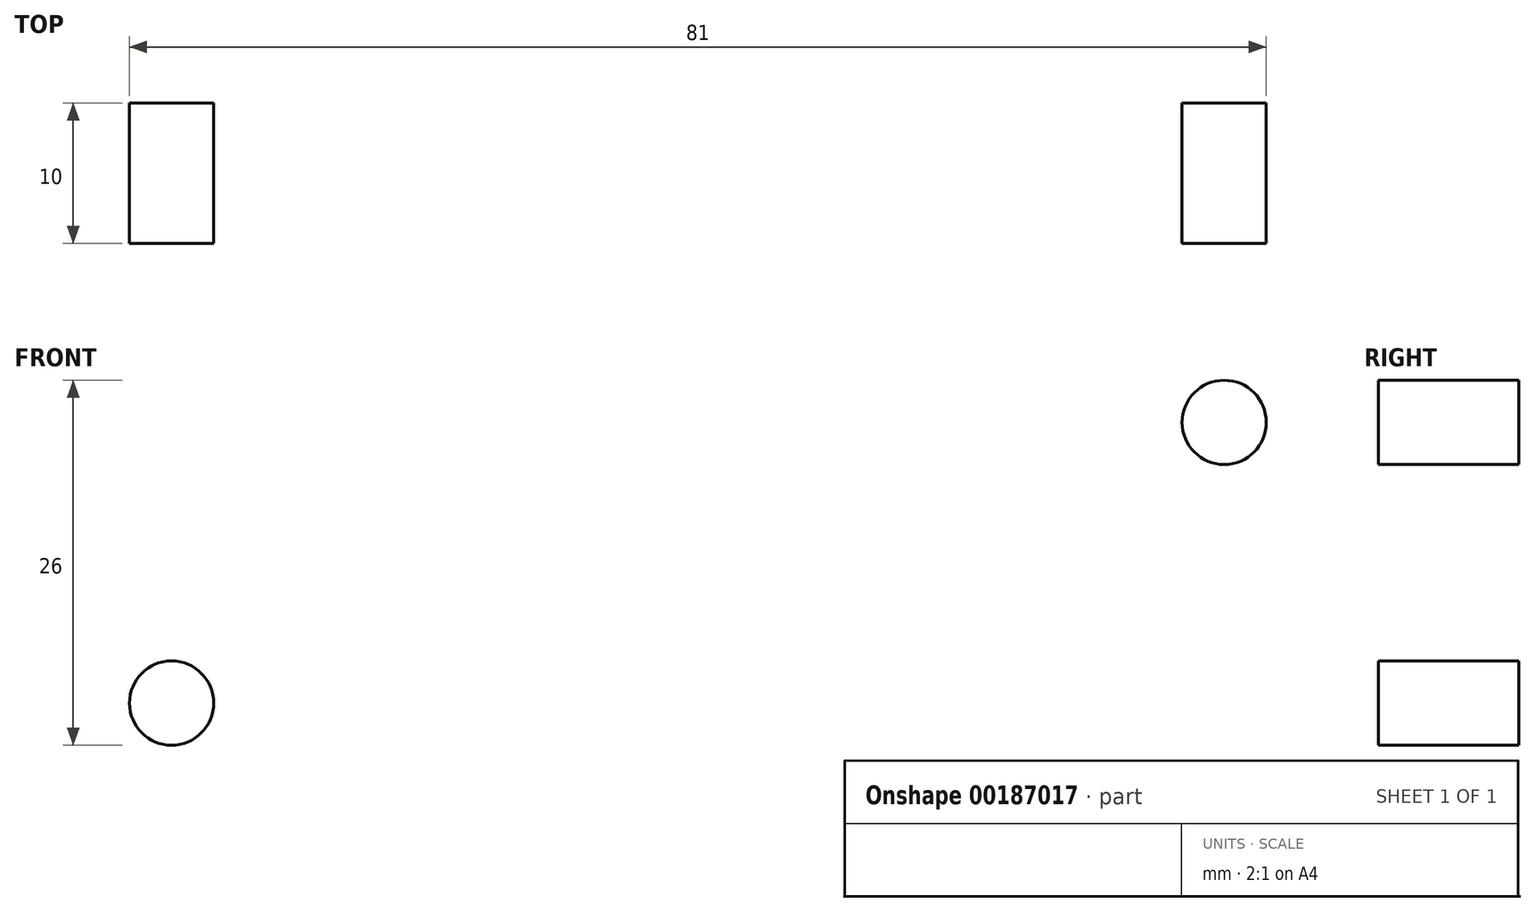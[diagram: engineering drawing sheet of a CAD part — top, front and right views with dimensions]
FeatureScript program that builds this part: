
annotation { "Feature Type Name" : "Feature", "Feature Type Description" : "" }
export const myFeature = defineFeature(function(context is Context, id is Id, definition is map)
    precondition{}
    {
        {
            var Q0;
            Q0=qCreatedBy(makeId("Front.planeOp"),FACE);
            var sketch = newSketch(context, id + "F0", { "sketchPlane" : qUnion([Q0])});
            skLineSegment(sketch, "E0.bottom", {"start": v(45, 17.5) * mm, "end": v(-45, 17.5) * mm});
            skLineSegment(sketch, "E0.top", {"start": v(45, -17.5) * mm, "end": v(-45, -17.5) * mm});
            skLineSegment(sketch, "E0.left", {"start": v(45, 17.5) * mm, "end": v(45, -17.5) * mm});
            skLineSegment(sketch, "E0.right", {"start": v(-45, 17.5) * mm, "end": v(-45, -17.5) * mm});
            skPoint(sketch, "E0.middle", {"position": v(0, 0) * mm});
            skSolve(sketch);
        }
        {
            var Q0;
            Q0=makeQuery(id+"F0.imprint","IMPRINT",FACE,{"disambiguationData":[TD([[makeQuery(id+"F0.imprint","IMPRINT",EDGE,{"derivedFrom":sQuery(id+"F0.wireOp",EDGE,"E0.bottom")}),1.0]])]});
            extrude(context, id + "F1", {"entities" : qUnion([Q0]), "depth" : 10 * mm});
        }
        {
            var Q0;
            Q0=makeQuery(id+"F1.opExtrude","CAP_FACE",FACE,{"disambiguationData":[OSD([sQuery(id+"F0.wireOp",EDGE,"E0.bottom"),sQuery(id+"F0.wireOp",EDGE,"E0.top"),sQuery(id+"F0.wireOp",EDGE,"E0.left"),sQuery(id+"F0.wireOp",EDGE,"E0.right")])],"isStart":false});
            var sketch = newSketch(context, id + "F2", { "sketchPlane" : qUnion([Q0])});
            skCircle(sketch, "E1", {"center": v(-23, 6.5) * mm, "radius": 2.5 * mm});
            skCircle(sketch, "E2", {"center": v(-23, -6.5) * mm, "radius": 2.5 * mm});
            skCircle(sketch, "E3.MirrorC", {"center": v(23, -6.5) * mm, "radius": 2.5 * mm});
            skCircle(sketch, "E4.MirrorC", {"center": v(23, 6.5) * mm, "radius": 2.5 * mm});
            skSolve(sketch);
        }
        {
            var Q0;
            Q0=makeQuery(id+"F1.opExtrude","CAP_FACE",FACE,{"disambiguationData":[OSD([sQuery(id+"F0.wireOp",EDGE,"E0.bottom"),sQuery(id+"F0.wireOp",EDGE,"E0.top"),sQuery(id+"F0.wireOp",EDGE,"E0.left"),sQuery(id+"F0.wireOp",EDGE,"E0.right")])],"isStart":false});
            var sketch = newSketch(context, id + "F3", { "sketchPlane" : qUnion([Q0])});
            skCircle(sketch, "E5", {"center": v(-37.5, 10) * mm, "radius": 3 * mm});
            skCircle(sketch, "E6.MirrorC", {"center": v(-37.5, -10) * mm, "radius": 3 * mm});
            skCircle(sketch, "E7.MirrorC", {"center": v(37.5, -10) * mm, "radius": 3 * mm});
            skCircle(sketch, "E8.MirrorC", {"center": v(37.5, 10) * mm, "radius": 3 * mm});
            skSolve(sketch);
        }
        {
            var Q0;
            Q0=makeQuery(id+"F3.imprint","IMPRINT",FACE,{"disambiguationData":[TD([[makeQuery(id+"F3.imprint","IMPRINT",EDGE,{"derivedFrom":sQuery(id+"F3.wireOp",EDGE,"E5")}),1.0]])]});
            var Q1;
            Q1=makeQuery(id+"F3.imprint","IMPRINT",FACE,{"disambiguationData":[TD([[makeQuery(id+"F3.imprint","IMPRINT",EDGE,{"derivedFrom":sQuery(id+"F3.wireOp",EDGE,"E6.MirrorC")}),-1.0]])]});
            var Q2;
            Q2=makeQuery(id+"F3.imprint","IMPRINT",FACE,{"disambiguationData":[TD([[makeQuery(id+"F3.imprint","IMPRINT",EDGE,{"derivedFrom":sQuery(id+"F3.wireOp",EDGE,"E7.MirrorC")}),1.0]])]});
            var Q3;
            Q3=makeQuery(id+"F3.imprint","IMPRINT",FACE,{"disambiguationData":[TD([[makeQuery(id+"F3.imprint","IMPRINT",EDGE,{"derivedFrom":sQuery(id+"F3.wireOp",EDGE,"E8.MirrorC")}),-1.0]])]});
            extrude(context, id + "F4", {"entities" : qUnion([Q0, Q1, Q2, Q3]), "operationType" : NewBodyOperationType.REMOVE, "endBound" : BoundingType.THROUGH_ALL, "oppositeDirection" : true, "depth" : 25 * mm});
        }
        {
            var Q0;
            Q0=sQuery(id+"F2.wireOp",VERTEX,"E1.center");
            var Q1;
            Q1=sQuery(id+"F2.wireOp",VERTEX,"E2.center");
            var Q2;
            Q2=sQuery(id+"F2.wireOp",VERTEX,"E3.MirrorC.center");
            var Q3;
            Q3=sQuery(id+"F2.wireOp",VERTEX,"E4.MirrorC.center");
            var Q4;
            Q4=makeQuery(id+"F1.opExtrude","SWEPT_BODY",BODY,{"disambiguationData":[OSD([sQuery(id+"F0.wireOp",EDGE,"E0.bottom"),sQuery(id+"F0.wireOp",EDGE,"E0.top"),sQuery(id+"F0.wireOp",EDGE,"E0.left"),sQuery(id+"F0.wireOp",EDGE,"E0.right")])]});
            hole(context, id + "F5", {"style" : HoleStyle.SIMPLE, "endStyle" : HoleEndStyle.BLIND, "standardTappedOrClearance" : lookupTablePath({ "standard" : "ISO", "fit" : "Close", "size" : "M6", "type" : "Clearance" }), "standardBlindInLast" : lookupTablePath({ "fit" : "Close", "standard" : "ISO", "size" : "M6", "type" : "Clearance" }), "holeDiameter" : 6.3 * mm, "holeDepth" : 20 * mm, "locations" : qUnion([Q0, Q1, Q2, Q3]), "scope" : qUnion([Q4])});
        }
    });
